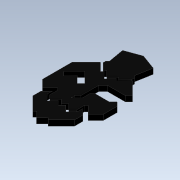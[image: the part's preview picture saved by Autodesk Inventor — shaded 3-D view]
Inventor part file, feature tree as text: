
AUTODESK INVENTOR PART (.ipt)
format: ipt  version: 2020 (Build 240168000, 168)  size: 288,256 bytes
history: native  units: in
note: dims shown in document units (in); Inventor stores cm internally (conversion verified against a paired STEP export)
features: extrude x1, sketch x1
ambient origin geometry x8: Origin, YZ Plane, XZ Plane, XY Plane, X Axis, Y Axis, Z Axis, Center Point
bodies: Solid1 (feature_tree)
feature tree (2):
  extrude  "Extrusion1"  TaperAngle=90.0deg  [1 undecoded]
  sketch  "Sketch1"  dims[d0=0.3937in d1=90.0deg d2=45.0deg d3=0.0394in d4=0.5906in d5=90.0deg d6=0.3937in d7=0.5906in d8=90.0deg d9=0.1969in d10=0.3937in d11=45.0deg d12=0.5906in d13=0.3937in d14=45.0deg d15=0.5906in d16=90.0deg d17=0.3937in d18=90.0deg d19=0.3937in d20=90.0deg d21=0.5906in d22=90.0deg d23=0.5906in d24=90.0deg d25=0.5906in d26=0.5906in d27=0.3937in d28=0.5906in d29=45.0deg d30=0.5906in d31=45.0deg d32=0.3937in d33=0.5906in d34=135.0deg d35=1.1811in d36=1.1811in d37=135.0deg d38=0.1969in d39=135.0deg d40=90.0deg d41=0.7874in d42=0.1969in d43=0.7874in d44=135.0deg d45=0.1969in d46=0.4331in d47=0.1969in d48=45.0deg d49=0.1969in d50=90.0deg d51=0.7874in d52=0.7874in d53=90.0deg d54=0.5906in d55=0.5906in d56=0.1969in d57=135.0deg d58=0.7297in d59=0.3937in d60=0.3937in d61=45.0deg d62=45.0deg d63=0.1532in d64=0.1969in d65=0.1969in d66=0.7874in d67=0.4752in d68=135.0deg d69=0.9843in d70=135.0deg d71=0.3868in d72=0.3937in d73=135.0deg d74=0.3937in d75=135.0deg d76=90.0deg d77=0.689in d78=0.689in d79=1.0827in d80=1.0827in d81=3.937in d82=135.0deg d83=45.0deg d84=1.1832in d85=1.1832in d86=90.0deg d87=0.5906in d88=5.4304in d89=2.6102in d90=0.1462in d91=0.8608in d92=0.7129in d93=3.8974in d94=0.1969in d95=0.4524in d96=0.4524in d97=0.1969in d98=0.1969in d99=45.0deg d100=0.5906in d101=45.0deg d102=0.5906in d103=90.0deg d104=0.1968in d105=90.0deg d106=0.7087in d107=0.7087in d108=2.7839in d109=0.1969in d110=0.1969in d111=0.1969in d112=135.0deg d113=135.0deg d114=0.1969in d115=1.1811in d116=0.8589in d117=0.6871in d118=1.2598in d119=0.8589in d120=1.1811in d121=0.6871in d122=0.3937in d123=0.0in]
note: 1 required parameter value undecoded (feature->parameter linkage not recoverable at this tier; creation-order binding heuristic only, values carry confidence <= 0.55)
